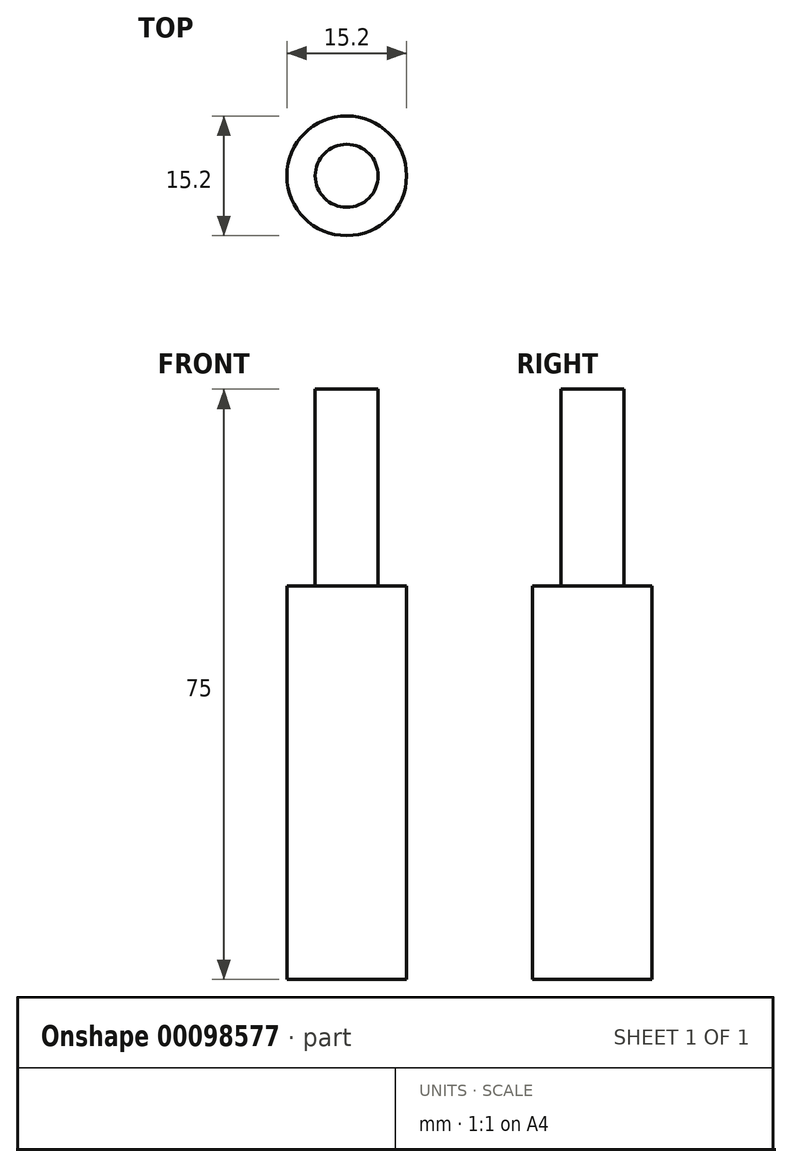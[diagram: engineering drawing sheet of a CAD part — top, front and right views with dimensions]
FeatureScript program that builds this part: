
annotation { "Feature Type Name" : "Feature", "Feature Type Description" : "" }
export const myFeature = defineFeature(function(context is Context, id is Id, definition is map)
    precondition{}
    {
        {
            var Q0;
            Q0=qCreatedBy(makeId("Top.planeOp"),FACE);
            var sketch = newSketch(context, id + "F0", { "sketchPlane" : qUnion([Q0])});
            skCircle(sketch, "E0", {"center": v(-47.13, 0) * mm, "radius": 7.6 * mm});
            skCircle(sketch, "E1", {"center": v(-47.13, 0) * mm, "radius": 4 * mm});
            skSolve(sketch);
        }
        {
            var Q0;
            Q0=makeQuery(id+"F0.imprint","IMPRINT",FACE,{"disambiguationData":[TD([[makeQuery(id+"F0.imprint","IMPRINT",EDGE,{"derivedFrom":sQuery(id+"F0.wireOp",EDGE,"E0")}),1.0]])]});
            var Q1;
            Q1=makeQuery(id+"F0.imprint","IMPRINT",FACE,{"disambiguationData":[TD([[makeQuery(id+"F0.imprint","IMPRINT",EDGE,{"derivedFrom":sQuery(id+"F0.wireOp",EDGE,"E1")}),1.0]])]});
            extrude(context, id + "F1", {"entities" : qUnion([Q0, Q1]), "oppositeDirection" : true, "depth" : 50 * mm});
        }
        {
            var Q0;
            Q0=makeQuery(id+"F0.imprint","IMPRINT",FACE,{"disambiguationData":[TD([[makeQuery(id+"F0.imprint","IMPRINT",EDGE,{"derivedFrom":sQuery(id+"F0.wireOp",EDGE,"E1")}),1.0]])]});
            extrude(context, id + "F2", {"entities" : qUnion([Q0]), "operationType" : NewBodyOperationType.ADD, "depth" : 25 * mm});
        }
        {
            var Q0;
            Q0=makeQuery(id+"F1.opExtrude","SWEPT_BODY",BODY,{"disambiguationData":[OSD([sQuery(id+"F0.wireOp",EDGE,"E0")])]});
            transform(context, id + "F3", {"entities" : qUnion([Q0]), "transformType" : TransformType.TRANSLATION_3D, "dx" : 0 * mm, "dy" : -5 * mm, "dz" : 25 * mm, "makeCopy" : false});
        }
    });
